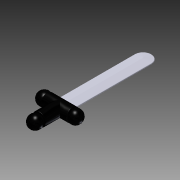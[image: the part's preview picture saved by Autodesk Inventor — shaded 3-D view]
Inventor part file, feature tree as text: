
AUTODESK INVENTOR PART (.ipt)
format: ipt  version: 2015 (Build 190159000, 159)  size: 171,008 bytes
history: native  units: mm
features: sketch x6, extrude x3, revolve x3, fillet x1
ambient origin geometry x8: Origin, YZ Plane, XZ Plane, XY Plane, X Axis, Y Axis, Z Axis, Center Point
bodies: Solid1 (feature_tree)
feature tree (13):
  extrude  "Extrusion1"  Depth=4.0mm TaperAngle=0.0deg
  extrude  "Extrusion2"  Depth=5.0mm TaperAngle=0.0deg
  revolve  "Revolution1"  [1 undecoded]
  revolve  "Revolution2"  [1 undecoded]
  fillet  "Fillet1"  Radius=0.5mm
  extrude  "Extrusion3"  TaperAngle=90.0deg  [1 undecoded]
  revolve  "Revolution5"  [1 undecoded]
  sketch  "Sketch1"  dims[d0=2.5mm d1=4.0mm d2=0.0mm]
  sketch  "Sketch2"  dims[d3=2.5mm d4=5.0mm d5=0.0mm]
  sketch  "Sketch3"  dims[d6=2.5mm d7=0.75mm]
  sketch  "Sketch4"  dims[d8=90.0deg d9=2.5mm d10=0.5mm]
  sketch  "Sketch5"  dims[d11=0.5mm d12=90.0deg]
  sketch  "Sketch9"  dims[d13=0.1mm d14=0.1mm d15=0.5mm d16=3.0mm d17=16.0mm d18=0.0mm d24=180.0deg]
note: 4 required parameter values undecoded (feature->parameter linkage not recoverable at this tier; creation-order binding heuristic only, values carry confidence <= 0.55)